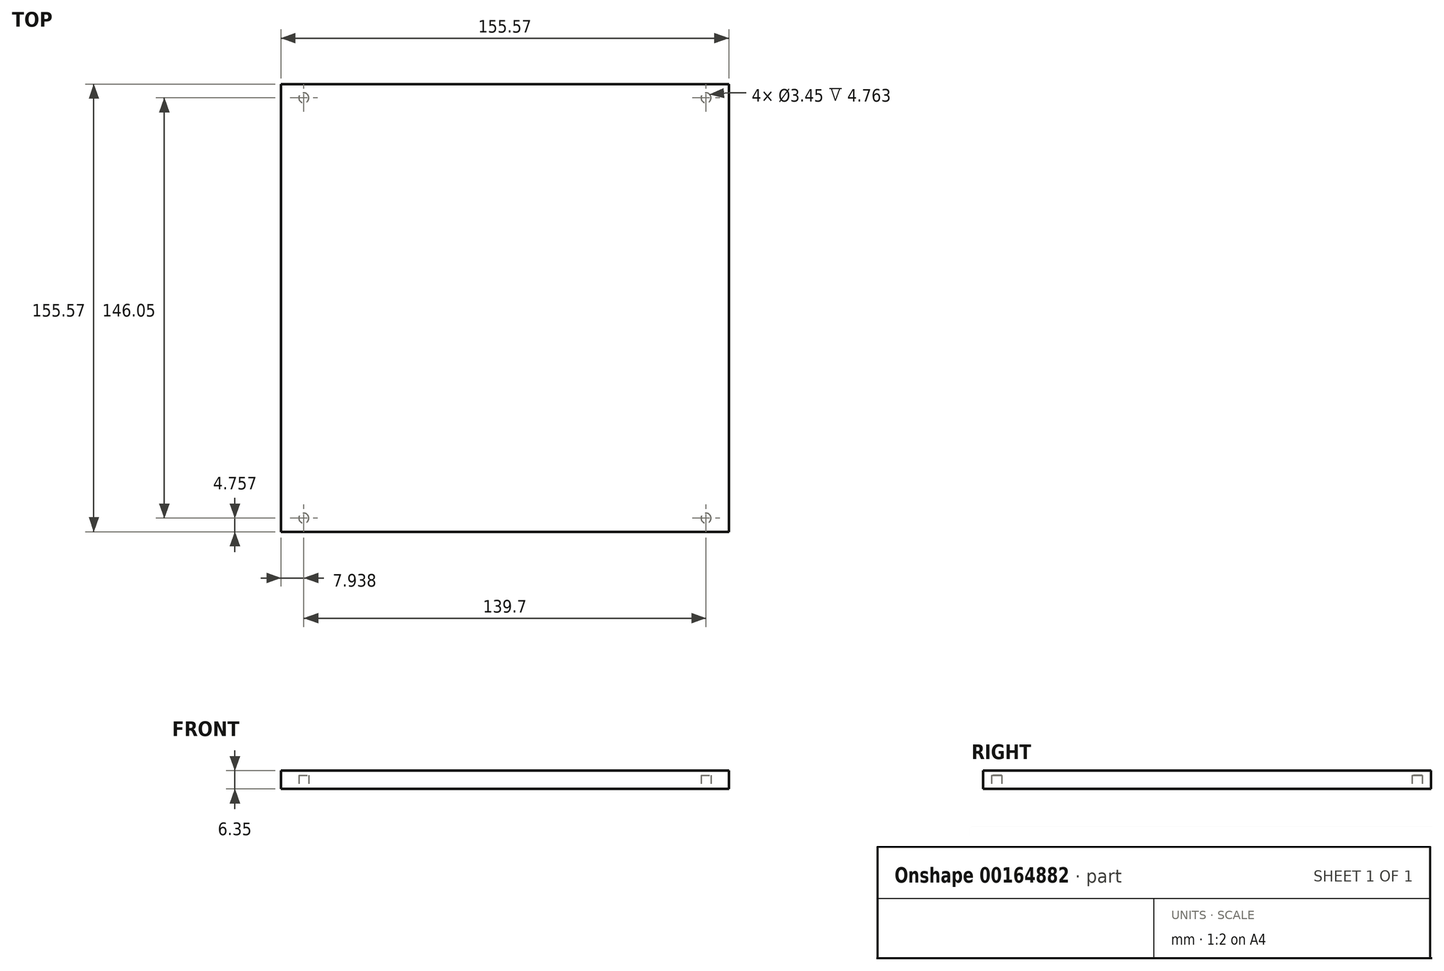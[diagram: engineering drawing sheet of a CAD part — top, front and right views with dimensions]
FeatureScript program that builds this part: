
annotation { "Feature Type Name" : "Feature", "Feature Type Description" : "" }
export const myFeature = defineFeature(function(context is Context, id is Id, definition is map)
    precondition{}
    {
        {
            var Q0;
            Q0=qCreatedBy(makeId("Top.planeOp"),FACE);
            var sketch = newSketch(context, id + "F0", { "sketchPlane" : qUnion([Q0])});
            skLineSegment(sketch, "E0.bottom", {"start": v(0, 0) * mm, "end": v(155.58, 0) * mm});
            skLineSegment(sketch, "E0.top", {"start": v(0, -155.58) * mm, "end": v(155.58, -155.58) * mm});
            skLineSegment(sketch, "E0.left", {"start": v(0, 0) * mm, "end": v(0, -155.58) * mm});
            skLineSegment(sketch, "E0.right", {"start": v(155.58, 0) * mm, "end": v(155.58, -155.58) * mm});
            skSolve(sketch);
        }
        {
            var Q0;
            Q0 = qSketchRegion(id + "F0", true);
            extrude(context, id + "F1", {"entities" : qUnion([Q0]), "depth" : 6.35 * mm});
        }
        {
            var Q0;
            Q0=makeQuery(id+"F1.opExtrude","CAP_FACE",FACE,{"disambiguationData":[OSD([sQuery(id+"F0.wireOp",EDGE,"E0.bottom"),sQuery(id+"F0.wireOp",EDGE,"E0.top"),sQuery(id+"F0.wireOp",EDGE,"E0.left"),sQuery(id+"F0.wireOp",EDGE,"E0.right")])],"isStart":true});
            var sketch = newSketch(context, id + "F2", { "sketchPlane" : qUnion([Q0])});
            skLineSegment(sketch, "E1", {"start": v(77.79, 155.58) * mm, "end": v(77.79, 0) * mm, "construction": true});
            skLineSegment(sketch, "E2.bottom", {"start": v(147.64, 150.81) * mm, "end": v(7.94, 150.81) * mm, "construction": true});
            skLineSegment(sketch, "E2.top", {"start": v(147.64, 4.76) * mm, "end": v(7.94, 4.76) * mm, "construction": true});
            skLineSegment(sketch, "E2.left", {"start": v(147.64, 150.81) * mm, "end": v(147.64, 4.76) * mm, "construction": true});
            skLineSegment(sketch, "E2.right", {"start": v(7.94, 150.81) * mm, "end": v(7.94, 4.76) * mm, "construction": true});
            skPoint(sketch, "E2.middle", {"position": v(77.79, 77.79) * mm});
            skLineSegment(sketch, "E3.bottom", {"start": v(147.64, 150.81) * mm, "end": v(155.58, 150.81) * mm, "construction": true});
            skLineSegment(sketch, "E3.top", {"start": v(147.64, 155.58) * mm, "end": v(155.58, 155.58) * mm, "construction": true});
            skLineSegment(sketch, "E3.left", {"start": v(147.64, 150.81) * mm, "end": v(147.64, 155.58) * mm, "construction": true});
            skLineSegment(sketch, "E3.right", {"start": v(155.58, 150.81) * mm, "end": v(155.58, 155.58) * mm, "construction": true});
            skCircle(sketch, "E4", {"center": v(147.64, 150.81) * mm, "radius": 1.73 * mm});
            skCircle(sketch, "E5", {"center": v(147.64, 4.76) * mm, "radius": 1.73 * mm});
            skCircle(sketch, "E6", {"center": v(7.94, 4.76) * mm, "radius": 1.73 * mm});
            skCircle(sketch, "E7", {"center": v(7.94, 150.81) * mm, "radius": 1.73 * mm});
            skSolve(sketch);
        }
        {
            var Q0;
            Q0 = qSketchRegion(id + "F2", true);
            extrude(context, id + "F3", {"entities" : qUnion([Q0]), "operationType" : NewBodyOperationType.REMOVE, "oppositeDirection" : true, "depth" : 4.76 * mm});
        }
    });
